# Revit family: Pressalit INDIVO Lift for worktop_Electrical
name_source: partatom
category: Specialty Equipment
units: mm (PartAtom-declared; Revit-internal decimal feet)

## family parameters
Always vertical = Yes
Cut with Voids When Loaded = No
Host = Wall
Maintain Annotation Orientation = No
Part Type = Normal
Room Calculation Point = No
Round Connector Dimension = Use Diameter
Shared = No

## types (20) — shared parameters
AdjustmentHeight = 300
ColourOptions = 000 White, 202 Grey
Electric = Yes
Fixed = No
Handle Offset Min = 110 mm  [stored 0.360892 ft]
Height Min = 645 mm  [stored 2.11614 ft]
Manufacturer = Pressalit A/S
ManufacturerName = Pressalit A/S
ManufacturerURL = https://pressalit.com
Material = Powder-coated steel, aluminium
NominalHeight = 645 mm  [stored 2.11614 ft]
NominalWidth = 535 mm  [stored 1.75525 ft]
Pressalit Product Series = INDIVO
RK111x = No
Size = L x 535 x 645
URL = https://pressalit.com
WarrantyDescription = Pressalit makes a commitment to remedy material and manufacturing defects for a period of five years from the invoicing date.
WarrantyDurationLabor = To be filled out by contractor.
WarrantyDurationParts = 3
WarrantyDurationUnit = Years
WarrantyGuarantorLabor = To be filled out by contractor.
WarrantyStartDate = Invoicing date.
Worktop Material = Pressalit - Worktop
Worktop Width Max = 700 mm  [stored 2.29659 ft]
Worktop Width Min = 600 mm
zero-valued in all types: Default Elevation, NominalLength

## per-type parameters (varying)
| type | Color | Description | Features | Frame Material | MainColor | MaximumLoad | Model | ModelNumber | ModelReference | NBSDescription | Name | ProductInformation | RK141x | RK145x | Version | Weight | Worktop Length Max | Worktop Length Min |
| RK1454000 | White | INDIVO lift for worktop 2401-3000 mm, electrically height adjustable, wall-mounted | Height adjustable up to 300 mm; from 645 - 945 mm, with switch or wired remote control (not included), length; 2401-3000 mm. | Pressalit - 000 White | White | 150 kg | RK1454 | RK1454 | RK1454 | INDIVO lift for worktop 2401-3000 mm, electrically height adjustable, wall-mounted | INDIVO lift for worktop, 2401-3000 mm | INDIVO lift for worktop, wall-mounted, with three motors and control box. Incl. cross brace and five brackets. Height adjustable up to 300 mm with switch or wired remote control (not included). For worktop length 2401-3000 mm. Excl. mounting kit. | No | Yes |  | 41 kg | 3000 mm  [stored 9.84252 ft] | 2401 mm  [stored 7.8773 ft] |
| RK1411202 | Grey | INDIVO lift for worktop 1001-1400 mm, electrically height adjustable, wall-mounted | Height adjustable up to 300 mm; from 645 - 945 mm, with switch or wired remote control (not included), length; 1001-1400 mm. | Pressalit - 202 White Aluminium | Grey | 100 kg | RK1411 | RK1411 | RK1411 | INDIVO lift for worktop 1001-1400 mm, electrically height adjustable, wall-mounted | INDIVO lift for worktop, 1001-1400 mm | INDIVO lift for worktop, wall-mounted, with two motors and control box. Incl. cross brace and two brackets. Height adjustable up to 300 mm with switch or wired remote control (not included). For worktop length 1001-1400 mm. Excl. mounting kit. | Yes | No |  | 30 kg | 1400 mm  [stored 4.59318 ft] | 1001 mm  [stored 3.28412 ft] |
| RK1413000 | White | INDIVO lift for worktop 2001-2400 mm, electrically height adjustable, wall-mounted | Height adjustable up to 300 mm; from 645 - 945 mm, with switch or wired remote control (not included), length; 2001-2400 mm. | Pressalit - 000 White | White | 100 kg | RK1413 | RK1413 | RK1413 | INDIVO lift for worktop 2001-2400 mm, electrically height adjustable, wall-mounted | INDIVO lift for worktop, 2001-2400 mm | INDIVO lift for worktop, wall-mounted, with two motors and control box. Incl. cross brace and four brackets. Height adjustable up to 300 mm with switch or wired remote control (not included). For worktop length 2001-2400 mm. Excl. mounting kit. | Yes | No |  | 37 kg | 2400 mm | 2001 mm |
| RK1450000 | White | INDIVO lift for worktop 600-1000 mm, electrically height adjustable, wall-mounted | Height adjustable up to 300 mm; from 645 - 945 mm, with switch or wired remote control (not included), length; 600-1000 mm. | Pressalit - 000 White | White | 150 kg | RK1450 | RK1450 | RK1450 | INDIVO lift for worktop 600-1000 mm, electrically height adjustable, wall-mounted | INDIVO lift for worktop, 600-1000 mm | INDIVO lift for worktop, wall-mounted, with three motors and control box. Incl. cross brace and two brackets. Height adjustable up to 300 mm with switch or wired remote control (not included). For worktop length 600-1000 mm. Excl. mounting kit. | No | Yes |  | 28 kg | 1000 mm  [stored 3.28084 ft] | 600 mm |
| RK1451000 | White | INDIVO lift for worktop 1001-1400 mm, electrically height adjustable, wall-mounted | Height adjustable up to 300 mm; from 645 - 945 mm, with switch or wired remote control (not included), length; 1001-1400 mm. | Pressalit - 000 White | White | 150 kg | RK1451 | RK1451 | RK1451 | INDIVO lift for worktop 1001-1400 mm, electrically height adjustable, wall-mounted | INDIVO lift for worktop, 1001-1400 mm | INDIVO lift for worktop, wall-mounted, with three motors and control box. Incl. cross brace and two brackets. Height adjustable up to 300 mm with switch or wired remote control (not included). For worktop length 1001-1400 mm. Excl. mounting kit. | No | Yes |  | 30 kg | 1400 mm  [stored 4.59318 ft] | 1001 mm  [stored 3.28412 ft] |
| RK1454202 | Grey | INDIVO lift for worktop 2401-3000 mm, electrically height adjustable, wall-mounted | Height adjustable up to 300 mm; from 645 - 945 mm, with switch or wired remote control (not included), length; 2401-3000 mm. | Pressalit - 202 White Aluminium | Grey | 150 kg | RK1454 | RK1454 | RK1454 | INDIVO lift for worktop 2401-3000 mm, electrically height adjustable, wall-mounted | INDIVO lift for worktop, 2401-3000 mm | INDIVO lift for worktop, wall-mounted, with three motors and control box. Incl. cross brace and five brackets. Height adjustable up to 300 mm with switch or wired remote control (not included). For worktop length 2401-3000 mm. Excl. mounting kit. | No | Yes |  | 41 kg | 3000 mm  [stored 9.84252 ft] | 2401 mm  [stored 7.8773 ft] |
| RK1411000 | White | INDIVO lift for worktop 1001-1400 mm, electrically height adjustable, wall-mounted | Height adjustable up to 300 mm; from 645 - 945 mm, with switch or wired remote control (not included), length; 1001-1400 mm. | Pressalit - 000 White | White | 100 kg | RK1411 | RK1411 | RK1411 | INDIVO lift for worktop 1001-1400 mm, electrically height adjustable, wall-mounted | INDIVO lift for worktop, 1001-1400 mm | INDIVO lift for worktop, wall-mounted, with two motors and control box. Incl. cross brace and two brackets. Height adjustable up to 300 mm with switch or wired remote control (not included). For worktop length 1001-1400 mm. Excl. mounting kit. | Yes | No |  | 30 kg | 1400 mm  [stored 4.59318 ft] | 1001 mm  [stored 3.28412 ft] |
| RK1413202 | Grey | INDIVO lift for worktop 2001-2400 mm, electrically height adjustable, wall-mounted | Height adjustable up to 300 mm; from 645 - 945 mm, with switch or wired remote control (not included), length; 2001-2400 mm. | Pressalit - 202 White Aluminium | Grey | 100 kg | RK1413 | RK1413 | RK1413 | INDIVO lift for worktop 2001-2400 mm, electrically height adjustable, wall-mounted | INDIVO lift for worktop, 2001-2400 mm | INDIVO lift for worktop, wall-mounted, with two motors and control box. Incl. cross brace and four brackets. Height adjustable up to 300 mm with switch or wired remote control (not included). For worktop length 2001-2400 mm. Excl. mounting kit. | Yes | No |  | 37 kg | 2400 mm | 2001 mm |
| RK1410202 | Grey | INDIVO lift for worktop 600-1000 mm, electrically height adjustable, wall-mounted | Height adjustable up to 300 mm; from 645 - 945 mm, with switch or wired remote control (not included), length; 600-1000 mm. | Pressalit - 202 White Aluminium | Grey | 100 kg | RK1410 | RK1410 | RK1410 | INDIVO lift for worktop 600-1000 mm, electrically height adjustable, wall-mounted | INDIVO lift for worktop, 600-1000 mm | INDIVO lift for worktop, wall-mounted, with two motors and control box. Incl. cross brace and two brackets. Height adjustable up to 300 mm with switch or wired remote control (not included). For worktop length 600-1000 mm. Excl. mounting kit. | Yes | No |  | 28 kg | 1000 mm  [stored 3.28084 ft] | 600 mm |
| RK1450202 | Grey | INDIVO lift for worktop 600-1000 mm, electrically height adjustable, wall-mounted | Height adjustable up to 300 mm; from 645 - 945 mm, with switch or wired remote control (not included), length; 600-1000 mm. | Pressalit - 202 White Aluminium | Grey | 150 kg | RK1450 | RK1450 | RK1450 | INDIVO lift for worktop 600-1000 mm, electrically height adjustable, wall-mounted | INDIVO lift for worktop, 600-1000 mm | INDIVO lift for worktop, wall-mounted, with three motors and control box. Incl. cross brace and two brackets. Height adjustable up to 300 mm with switch or wired remote control (not included). For worktop length 600-1000 mm. Excl. mounting kit. | No | Yes |  | 28 kg | 1000 mm  [stored 3.28084 ft] | 600 mm |
| RK1451202 | Grey | INDIVO lift for worktop 1001-1400 mm, electrically height adjustable, wall-mounted | Height adjustable up to 300 mm; from 645 - 945 mm, with switch or wired remote control (not included), length; 1001-1400 mm. | Pressalit - 202 White Aluminium | Grey | 150 kg | RK1451 | RK1451 | RK1451 | INDIVO lift for worktop 1001-1400 mm, electrically height adjustable, wall-mounted | INDIVO lift for worktop, 1001-1400 mm | INDIVO lift for worktop, wall-mounted, with three motors and control box. Incl. cross brace and two brackets. Height adjustable up to 300 mm with switch or wired remote control (not included). For worktop length 1001-1400 mm. Excl. mounting kit. | No | Yes |  | 30 kg | 1400 mm  [stored 4.59318 ft] | 1001 mm  [stored 3.28412 ft] |
| RK1414202 | Grey | INDIVO lift for worktop 2401-3000 mm, electrically height adjustable, wall-mounted | Height adjustable up to 300 mm; from 645 - 945 mm, with switch or wired remote control (not included), length; 2401-3000 mm. | Pressalit - 202 White Aluminium | Grey | 100 kg | RK1414 | RK1414 | RK1414 | INDIVO lift for worktop 2401-3000 mm, electrically height adjustable, wall-mounted | INDIVO lift for worktop, 2401-3000 mm | INDIVO lift for worktop, wall-mounted, with two motors and control box. Incl. cross brace and five brackets. Height adjustable up to 300 mm with switch or wired remote control (not included). For worktop length 2401-3000 mm. Excl. mounting kit. | Yes | No |  | 41 kg | 3000 mm  [stored 9.84252 ft] | 2401 mm  [stored 7.8773 ft] |
| RK1452202 | Grey | INDIVO lift for worktop 1401-2000 mm, electrically height adjustable, wall-mounted | Height adjustable up to 300 mm; from 645 - 945 mm, with switch or wired remote control (not included), length; 1401-2000 mm. | Pressalit - 202 White Aluminium | Grey | 150 kg | RK1452 | RK1452 | RK1452 | INDIVO lift for worktop 1401-2000 mm, electrically height adjustable, wall-mounted | INDIVO lift for worktop, 1401-2000 mm | INDIVO lift for worktop, wall-mounted, with three motors and control box. Incl. cross brace and three brackets. Height adjustable up to 300 mm with switch or wired remote control (not included). For worktop length 1401-2000 mm. Excl. mounting kit. | No | Yes | 2022-04-29 | 34 kg | 2000 mm  [stored 6.56168 ft] | 1401 mm |
| RK1452000 | White | INDIVO lift for worktop 1401-2000 mm, electrically height adjustable, wall-mounted | Height adjustable up to 300 mm; from 645 - 945 mm, with switch or wired remote control (not included), length; 1401-2000 mm. | Pressalit - 000 White | White | 150 kg | RK1452 | RK1452 | RK1452 | INDIVO lift for worktop 1401-2000 mm, electrically height adjustable, wall-mounted | INDIVO lift for worktop, 1401-2000 mm | INDIVO lift for worktop, wall-mounted, with three motors and control box. Incl. cross brace and three brackets. Height adjustable up to 300 mm with switch or wired remote control (not included). For worktop length 1401-2000 mm. Excl. mounting kit. | No | Yes | 2022-04-29 | 34 kg | 2000 mm  [stored 6.56168 ft] | 1401 mm |
| RK1410000 | White | INDIVO lift for worktop 600-1000 mm, electrically height adjustable, wall-mounted | Height adjustable up to 300 mm; from 645 - 945 mm, with switch or wired remote control (not included), length; 600-1000 mm. | Pressalit - 000 White | White | 100 kg | RK1410 | RK1410 | RK1410 | INDIVO lift for worktop 600-1000 mm, electrically height adjustable, wall-mounted | INDIVO lift for worktop, 600-1000 mm | INDIVO lift for worktop, wall-mounted, with two motors and control box. Incl. cross brace and two brackets. Height adjustable up to 300 mm with switch or wired remote control (not included). For worktop length 600-1000 mm. Excl. mounting kit. | Yes | No | 2022-04-29 | 28 kg | 1000 mm  [stored 3.28084 ft] | 600 mm |
| RK1414000 | White | INDIVO lift for worktop 2401-3000 mm, electrically height adjustable, wall-mounted | Height adjustable up to 300 mm; from 645 - 945 mm, with switch or wired remote control (not included), length; 2401-3000 mm. | Pressalit - 000 White | White | 100 kg | RK1414 | RK1414 | RK1414 | INDIVO lift for worktop 2401-3000 mm, electrically height adjustable, wall-mounted | INDIVO lift for worktop, 2401-3000 mm | INDIVO lift for worktop, wall-mounted, with two motors and control box. Incl. cross brace and five brackets. Height adjustable up to 300 mm with switch or wired remote control (not included). For worktop length 2401-3000 mm. Excl. mounting kit. | Yes | No | 2022-04-29 | 41 kg | 3000 mm  [stored 9.84252 ft] | 2401 mm  [stored 7.8773 ft] |
| RK1453000 | White | INDIVO lift for worktop 2001-2400 mm, electrically height adjustable, wall-mounted | Height adjustable up to 300 mm; from 645 - 945 mm, with switch or wired remote control (not included), length; 2001-2400 mm. | Pressalit - 000 White | White | 150 kg | RK1453 | RK1453 | RK1453 | INDIVO lift for worktop 2001-2400 mm, electrically height adjustable, wall-mounted | INDIVO lift for worktop, 2001-2400 mm | INDIVO lift for worktop, wall-mounted, with three motors and control box. Incl. cross brace and four brackets. Height adjustable up to 300 mm with switch or wired remote control (not included). For worktop length 2001-2400 mm. Excl. mounting kit. | No | Yes | 2022-04-29 | 37 kg | 2400 mm | 2001 mm |
| RK1412202 | Grey | INDIVO lift for worktop 1401-2000 mm, electrically height adjustable, wall-mounted | Height adjustable up to 300 mm; from 645 - 945 mm, with switch or wired remote control (not included), length; 1401-2000 mm. | Pressalit - 202 White Aluminium | Grey | 100 kg | RK1412 | RK1412 | RK1412 | INDIVO lift for worktop 1401-2000 mm, electrically height adjustable, wall-mounted | INDIVO lift for worktop, 1401-2000 mm | INDIVO lift for worktop, wall-mounted, with two motors and control box. Incl. cross brace and three brackets. Height adjustable up to 300 mm with switch or wired remote control (not included). For worktop length 1401-2000 mm. Excl. mounting kit. | Yes | No | 2022-04-29 | 34 kg | 2000 mm  [stored 6.56168 ft] | 1401 mm |
| RK1412000 | White | INDIVO lift for worktop 1401-2000 mm, electrically height adjustable, wall-mounted | Height adjustable up to 300 mm; from 645 - 945 mm, with switch or wired remote control (not included), length; 1401-2000 mm. | Pressalit - 000 White | White | 100 kg | RK1412 | RK1412 | RK1412 | INDIVO lift for worktop 1401-2000 mm, electrically height adjustable, wall-mounted | INDIVO lift for worktop, 1401-2000 mm | INDIVO lift for worktop, wall-mounted, with two motors and control box. Incl. cross brace and three brackets. Height adjustable up to 300 mm with switch or wired remote control (not included). For worktop length 1401-2000 mm. Excl. mounting kit. | Yes | No | 2022-04-29 | 34 kg | 2000 mm  [stored 6.56168 ft] | 1401 mm |
| RK1453202 | Grey | INDIVO lift for worktop 2001-2400 mm, electrically height adjustable, wall-mounted | Height adjustable up to 300 mm; from 645 - 945 mm, with switch or wired remote control (not included), length; 2001-2400 mm. | Pressalit - 202 White Aluminium | Grey | 150 kg | RK1453 | RK1453 | RK1453 | INDIVO lift for worktop 2001-2400 mm, electrically height adjustable, wall-mounted | INDIVO lift for worktop, 2001-2400 mm | INDIVO lift for worktop, wall-mounted, with three motors and control box. Incl. cross brace and four brackets. Height adjustable up to 300 mm with switch or wired remote control (not included). For worktop length 2001-2400 mm. Excl. mounting kit. | No | Yes | 2022-04-29 | 37 kg | 2400 mm | 2001 mm |

note: column(s) folded — value = type name in every type: Pressalit Product Number

note: [stored X ft] marks values corroborated as IEEE doubles in the binary element streams (Revit-internal decimal feet)

## geometry (parser evidence)
native form markers: Sweep x16
no freeform markers — native parametric forms only
